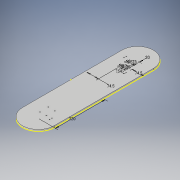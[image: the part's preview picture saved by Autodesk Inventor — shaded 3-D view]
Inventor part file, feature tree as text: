
AUTODESK INVENTOR PART (.ipt)
format: ipt  version: 2019 (Build 230136000, 136)  size: 156,160 bytes
history: native  units: mm
features: sketch x5, hole x4, other x1, extrude x1
ambient origin geometry x8: Origin, YZ Plane, XZ Plane, XY Plane, X Axis, Y Axis, Z Axis, Center Point
bodies: Body1 (feature_tree)
feature tree (11):
  other  "ソリッド1"
  sketch  "スケッチ1"
  extrude  "押し出し1"  Depth=270.0mm
  sketch  "スケッチ4"
  hole  "穴2"  [1 undecoded]
  hole  "穴3"  [1 undecoded]
  hole  "穴4"  [1 undecoded]
  hole  "穴5"  [1 undecoded]
  sketch  "スケッチ2"
  sketch  "スケッチ6"
  sketch  "スケッチ7"
note: 4 required parameter values undecoded (feature->parameter linkage not recoverable at this tier; creation-order binding heuristic only, values carry confidence <= 0.55)
